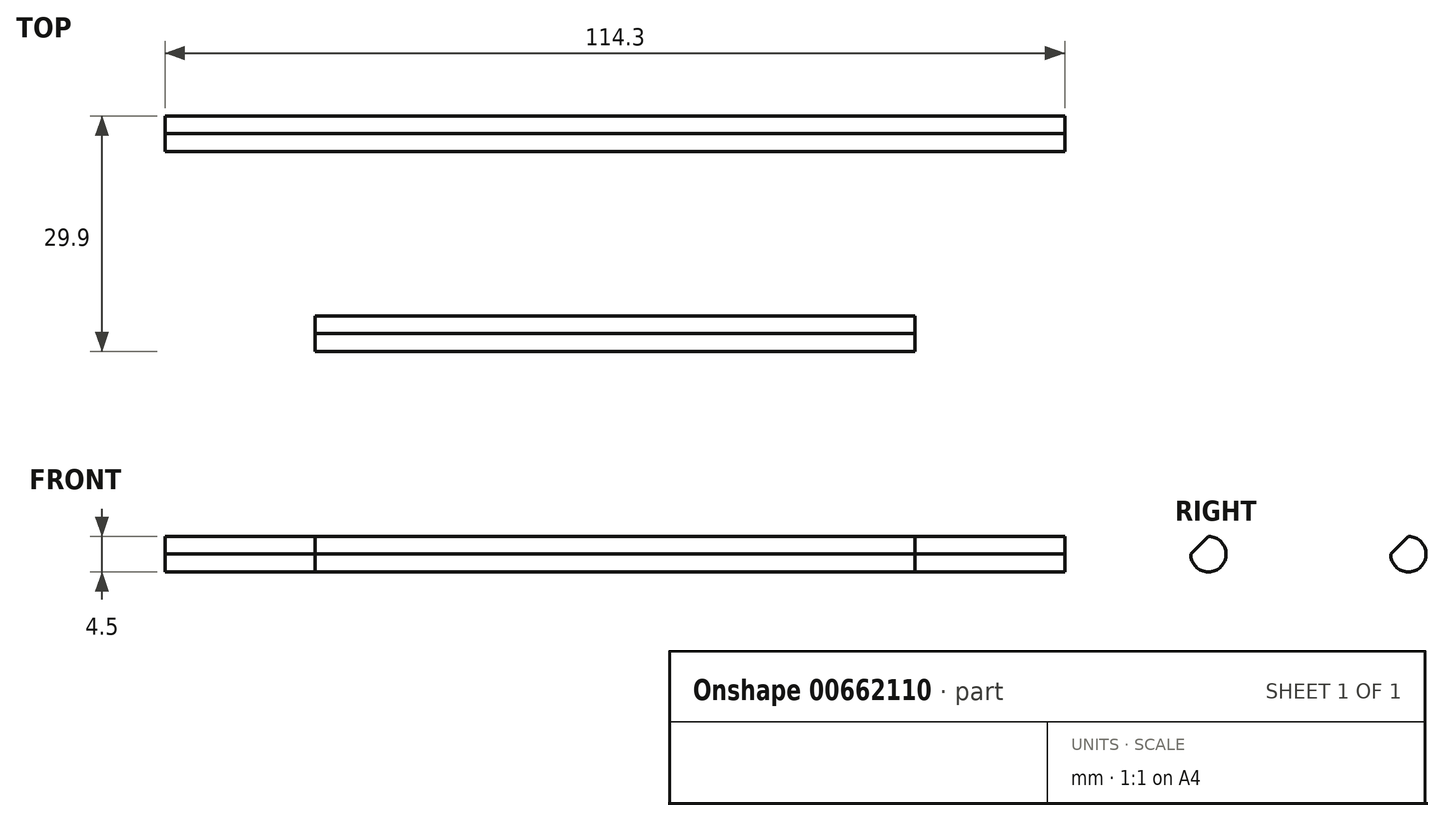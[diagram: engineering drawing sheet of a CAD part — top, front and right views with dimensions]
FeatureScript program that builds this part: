
annotation { "Feature Type Name" : "Feature", "Feature Type Description" : "" }
export const myFeature = defineFeature(function(context is Context, id is Id, definition is map)
    precondition{}
    {
        {
            var Q0;
            Q0=qCreatedBy(makeId("Right.planeOp"),FACE);
            var sketch = newSketch(context, id + "F0", { "sketchPlane" : qUnion([Q0])});
            skCircle(sketch, "E0", {"center": v(0, 0) * mm, "radius": 2.25 * mm});
            skLineSegment(sketch, "E1", {"start": v(0, 2.25) * mm, "end": v(-2.25, 0) * mm});
            skSolve(sketch);
        }
        {
            var Q0;
            {var subQ0=sQuery(id+"F0.wireOp",EDGE,"E1");Q0=makeQuery(id+"F0.imprint","IMPRINT",FACE,{"disambiguationData":[TD([[makeQuery(id+"F0.imprint","IMPRINT",EDGE,{"derivedFrom":subQ0}),1.0]])]});}
            extrude(context, id + "F1", {"entities" : qUnion([Q0]), "endBound" : BoundingType.SYMMETRIC, "depth" : 114.3 * mm, "offsetDistance" : 25.4 * mm});
        }
        {
            var Q0;
            Q0=makeQuery(id+"F1.opExtrude","SWEPT_BODY",BODY,{"disambiguationData":[OSD([sQuery(id+"F0.wireOp",EDGE,"E0"),sQuery(id+"F0.wireOp",EDGE,"E1")])]});
            var Q1;
            Q1=qCreatedBy(makeId("Front.planeOp"),FACE);
            transform(context, id + "F2", {"entities" : qUnion([Q0]), "transformType" : TransformType.TRANSLATION_DISTANCE, "transformDirection" : qUnion([Q1]), "distance" : 25.4 * mm, "makeCopy" : true});
        }
        {
            var Q0;
            Q0=makeQuery(id+"F2.opPattern","COPY",FACE,{"derivedFrom":makeQuery(id+"F1.opExtrude","CAP_FACE",FACE,{"disambiguationData":[OSD([sQuery(id+"F0.wireOp",EDGE,"E0"),sQuery(id+"F0.wireOp",EDGE,"E1")])],"isStart":false}),"instanceName":"1"});
            extrude(context, id + "F3", {"entities" : qUnion([Q0]), "operationType" : NewBodyOperationType.REMOVE, "oppositeDirection" : true, "depth" : 19.05 * mm, "offsetDistance" : 25.4 * mm});
        }
        {
            var Q0;
            Q0=makeQuery(id+"F2.opPattern","COPY",FACE,{"derivedFrom":makeQuery(id+"F1.opExtrude","CAP_FACE",FACE,{"disambiguationData":[OSD([sQuery(id+"F0.wireOp",EDGE,"E0"),sQuery(id+"F0.wireOp",EDGE,"E1")])],"isStart":true}),"instanceName":"1"});
            extrude(context, id + "F4", {"entities" : qUnion([Q0]), "operationType" : NewBodyOperationType.REMOVE, "oppositeDirection" : true, "depth" : 19.05 * mm, "offsetDistance" : 25.4 * mm});
        }
    });
